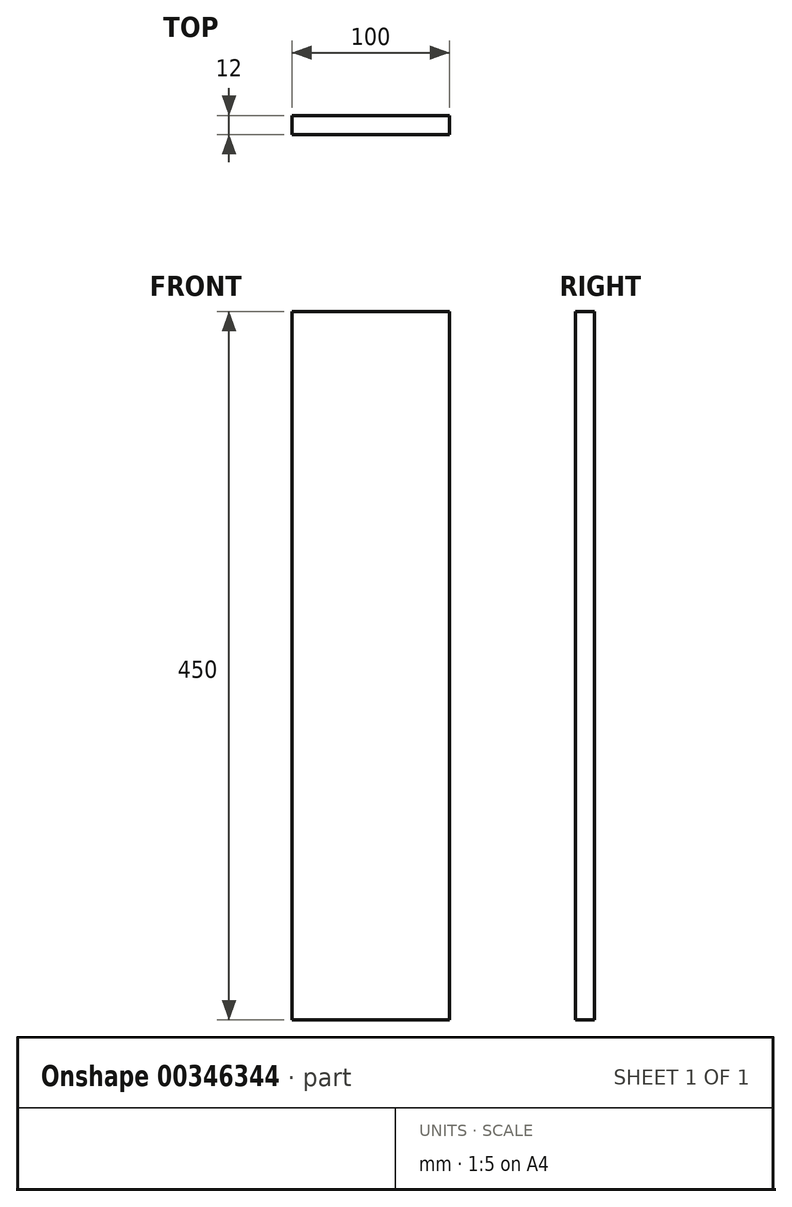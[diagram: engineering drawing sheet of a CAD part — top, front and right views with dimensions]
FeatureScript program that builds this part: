
annotation { "Feature Type Name" : "Feature", "Feature Type Description" : "" }
export const myFeature = defineFeature(function(context is Context, id is Id, definition is map)
    precondition{}
    {
        {
            var Q0;
            Q0=qCreatedBy(makeId("Front.planeOp"),FACE);
            var sketch = newSketch(context, id + "F0", { "sketchPlane" : qUnion([Q0])});
            skLineSegment(sketch, "E0.bottom", {"start": v(50, 225) * mm, "end": v(-50, 225) * mm});
            skLineSegment(sketch, "E0.top", {"start": v(50, -225) * mm, "end": v(-50, -225) * mm});
            skLineSegment(sketch, "E0.left", {"start": v(50, 225) * mm, "end": v(50, -225) * mm});
            skLineSegment(sketch, "E0.right", {"start": v(-50, 225) * mm, "end": v(-50, -225) * mm});
            skPoint(sketch, "E0.middle", {"position": v(0, 0) * mm});
            skSolve(sketch);
        }
        {
            var Q0;
            Q0=makeQuery(id+"F0.imprint","IMPRINT",FACE,{"disambiguationData":[TD([[makeQuery(id+"F0.imprint","IMPRINT",EDGE,{"derivedFrom":sQuery(id+"F0.wireOp",EDGE,"E0.bottom")}),1.0]])]});
            extrude(context, id + "F1", {"entities" : qUnion([Q0]), "endBound" : BoundingType.SYMMETRIC, "depth" : 12 * mm});
        }
    });
